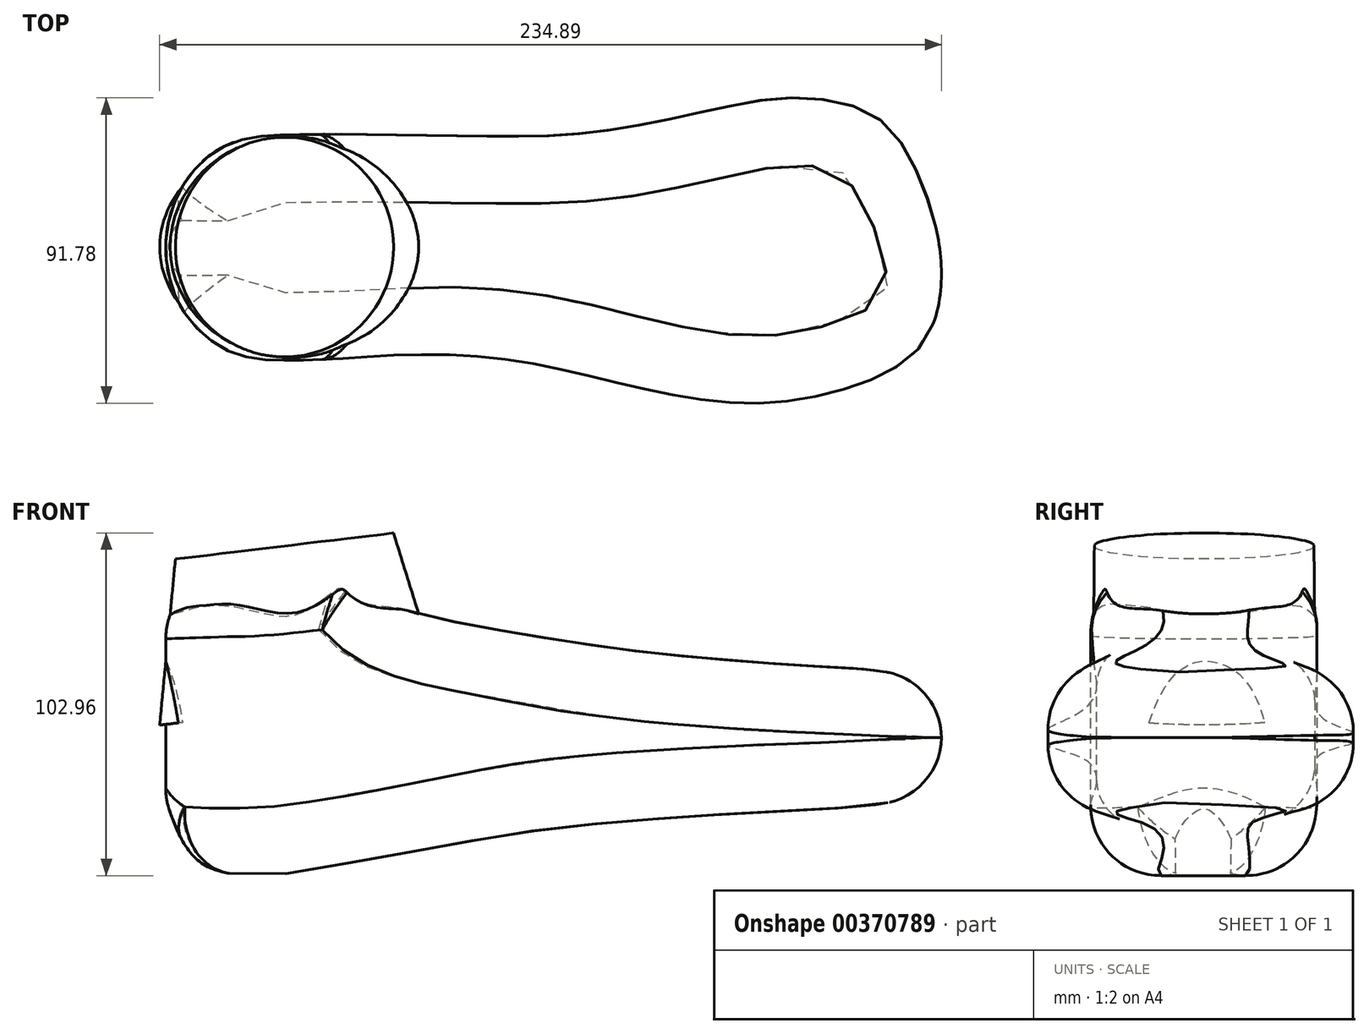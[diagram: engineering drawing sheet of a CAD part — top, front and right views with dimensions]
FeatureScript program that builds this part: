
annotation { "Feature Type Name" : "Feature", "Feature Type Description" : "" }
export const myFeature = defineFeature(function(context is Context, id is Id, definition is map)
    precondition{}
    {
        {
            var Q0;
            Q0=qCreatedBy(makeId("Top.planeOp"),FACE);
            cPlane(context, id + "F0", {"entities" : qUnion([Q0]), "cplaneType" : CPlaneType.OFFSET, "offset" : 10 * mm, "oppositeDirection" : true, "width" : 150 * mm, "height" : 150 * mm});
        }
        {
            var Q0;
            Q0=qCreatedBy(makeId("Front.planeOp"),FACE);
            var sketch = newSketch(context, id + "F1", { "sketchPlane" : qUnion([Q0])});
            skLineSegment(sketch, "E0", {"start": v(-126.2, 34.59) * mm, "end": v(0, 49.64) * mm, "construction": true});
            skSolve(sketch);
        }
        {
            var Q0;
            Q0=qCreatedBy(makeId("Right.planeOp"),FACE);
            var sketch = newSketch(context, id + "F2", { "sketchPlane" : qUnion([Q0])});
            skLineSegment(sketch, "E1.0", {"start": v(0, 34.59) * mm, "end": v(0, 49.64) * mm, "construction": true});
            skLineSegment(sketch, "E2", {"start": v(0, 49.64) * mm, "end": v(78.18, 49.64) * mm, "construction": true});
            skSolve(sketch);
        }
        {
            var Q0;
            Q0=sQuery(id+"F2.wireOp",VERTEX,"E2.end");
            var Q1;
            Q1=sQuery(id+"F2.wireOp",VERTEX,"E2.start");
            var Q2;
            Q2=sQuery(id+"F1.wireOp",VERTEX,"E0.start");
            cPlane(context, id + "F3", {"entities" : qUnion([Q0, Q1, Q2]), "cplaneType" : CPlaneType.THREE_POINT, "offset" : 25 * mm, "width" : 150 * mm, "height" : 150 * mm});
        }
        {
            var Q0;
            Q0=qCreatedBy(id+"F0.planeOp",FACE);
            cPlane(context, id + "F4", {"entities" : qUnion([Q0]), "cplaneType" : CPlaneType.OFFSET, "offset" : 70 * mm, "width" : 150 * mm, "height" : 150 * mm});
        }
        {
            var Q0;
            Q0=qCreatedBy(id+"F4.planeOp",FACE);
            var sketch = newSketch(context, id + "F5", { "sketchPlane" : qUnion([Q0])});
            skLineSegment(sketch, "E3.bottom", {"start": v(178, 87.04) * mm, "end": v(-168.77, 87.04) * mm});
            skLineSegment(sketch, "E3.top", {"start": v(178, -71.84) * mm, "end": v(-168.77, -71.84) * mm});
            skLineSegment(sketch, "E3.left", {"start": v(178, 87.04) * mm, "end": v(178, -71.84) * mm});
            skLineSegment(sketch, "E3.right", {"start": v(-168.77, 87.04) * mm, "end": v(-168.77, -71.84) * mm});
            skFitSpline(sketch, "E4", {"points": [v(111.8, -41.46) * mm, v(125.03, -30.87) * mm, v(130.33, -15.25) * mm, v(129.4, 3.7) * mm, v(122.2, 25.52) * mm, v(108.35, 43.13) * mm, v(83.24, 48.74) * mm, v(61.9, 46.12) * mm, v(19.97, 37.89) * mm, v(-18.8, 36.21) * mm, v(-53.4, 36.76) * mm, v(-76.61, 36.81) * mm, v(-99.24, 34.61) * mm, v(-114.06, 24.29) * mm, v(-122.11, 6.16) * mm, v(-120.89, -12.02) * mm, v(-114.25, -24.52) * mm, v(-104.4, -32.8) * mm, v(-93.42, -36.4) * mm, v(-70, -36.67) * mm, v(-39.87, -35.1) * mm, v(-3.08, -38.02) * mm, v(40.33, -47.81) * mm, v(79.5, -50.46) * mm, v(111.8, -41.46) * mm]});
            skSolve(sketch);
        }
        {
            var Q0;
            Q0=qCreatedBy(makeId("Front.planeOp"),FACE);
            var sketch = newSketch(context, id + "F6", { "sketchPlane" : qUnion([Q0])});
            skFitSpline(sketch, "E5", {"points": [v(-119.13, 38.44) * mm, v(-119.13, 33.94) * mm, v(-120.9, 4.27) * mm, v(-123.57, -25.48) * mm, v(-120.92, -39.45) * mm, v(-113.66, -52.87) * mm, v(-104.36, -58.06) * mm, v(-92.75, -59.32) * mm, v(-77.53, -57.75) * mm, v(-27.63, -48.8) * mm, v(12.86, -42.84) * mm, v(69.82, -38.75) * mm, v(100.89, -37.03) * mm, v(116.9, -34.52) * mm, v(127.68, -28.43) * mm, v(131.34, -21.72) * mm, v(132.41, -11.5) * mm, v(130.12, -3.1) * mm, v(121.42, 4.53) * mm, v(108.1, 7.85) * mm, v(96.18, 8.64) * mm, v(56.48, 11.46) * mm, v(17.18, 15.9) * mm, v(-22.2, 22.42) * mm, v(-50.23, 30.16) * mm, v(-57.52, 38.83) * mm, v(-59.94, 45.04) * mm, v(-66.68, 44.3) * mm, v(-113.57, 39.24) * mm, v(-119.13, 38.44) * mm]});
            skSolve(sketch);
        }
        {
            var Q0;
            Q0=qSketchRegion(id+"F6",true);
            extrude(context, id + "F7", {"entities" : qUnion([Q0]), "depth" : 140 * mm, "symmetric" : true});
        }
        {
            var Q0;
            Q0=makeQuery(id+"F5.imprint","IMPRINT",FACE,{"disambiguationData":[TD([[makeQuery(id+"F5.imprint","IMPRINT",EDGE,{"derivedFrom":sQuery(id+"F5.wireOp",EDGE,"E3.bottom")}),1.0]])]});
            extrude(context, id + "F8", {"entities" : qUnion([Q0]), "operationType" : NewBodyOperationType.REMOVE, "oppositeDirection" : true, "depth" : 130 * mm});
        }
        {
            var Q0;
            Q0=makeQuery(id+"F8.boolean.opBoolean","INTERSECT",EDGE,{"disambiguationData":[OD(1.0)],"derivedFrom":[makeQuery(id+"F7.opExtrude","SWEPT_FACE",FACE,{"disambiguationData":[OSD([sQuery(id+"F6.wireOp",EDGE,"E5")])]}),makeQuery(id+"F8.opExtrude","SWEPT_FACE",FACE,{"disambiguationData":[OSD([sQuery(id+"F5.wireOp",EDGE,"E4")])]})]});
            fillet(context, id + "F9", {"entities" : qUnion([Q0]), "radius" : 22 * mm, "allowEdgeOverflow" : false});
        }
        {
            var Q0;
            Q0=makeQuery(id+"F8.boolean.opBoolean","INTERSECT",EDGE,{"disambiguationData":[OD(0.0)],"derivedFrom":[makeQuery(id+"F7.opExtrude","SWEPT_FACE",FACE,{"disambiguationData":[OSD([sQuery(id+"F6.wireOp",EDGE,"E5")])]}),makeQuery(id+"F8.opExtrude","SWEPT_FACE",FACE,{"disambiguationData":[OSD([sQuery(id+"F5.wireOp",EDGE,"E4")])]})]});
            fillet(context, id + "F10", {"entities" : qUnion([Q0]), "radius" : 22 * mm, "tangentPropagation" : true, "allowEdgeOverflow" : false});
        }
        {
            var Q0;
            Q0=qCreatedBy(id+"F3.planeOp",FACE);
            var sketch = newSketch(context, id + "F11", { "sketchPlane" : qUnion([Q0])});
            skLineSegment(sketch, "E6.bottom", {"start": v(-167.37, -58.49) * mm, "end": v(31.87, -58.49) * mm});
            skLineSegment(sketch, "E6.top", {"start": v(-167.37, 81.96) * mm, "end": v(31.87, 81.96) * mm});
            skLineSegment(sketch, "E6.left", {"start": v(-167.37, -58.49) * mm, "end": v(-167.37, 81.96) * mm});
            skLineSegment(sketch, "E6.right", {"start": v(31.87, -58.49) * mm, "end": v(31.87, 81.96) * mm});
            skSolve(sketch);
        }
        {
            var Q0;
            Q0=makeQuery(id+"F11.imprint","IMPRINT",FACE,{"disambiguationData":[TD([[makeQuery(id+"F11.imprint","IMPRINT",EDGE,{"derivedFrom":sQuery(id+"F11.wireOp",EDGE,"E6.bottom")}),1.0]])]});
            extrude(context, id + "F12", {"entities" : qUnion([Q0]), "operationType" : NewBodyOperationType.REMOVE, "depth" : 10 * mm, "symmetric" : true});
        }
        {
            var Q0;
            Q0=qCreatedBy(id+"F3.planeOp",FACE);
            cPlane(context, id + "F13", {"entities" : qUnion([Q0]), "cplaneType" : CPlaneType.OFFSET, "offset" : 96 * mm, "oppositeDirection" : true, "width" : 150 * mm, "height" : 150 * mm});
        }
        {
            var Q0;
            Q0=qCreatedBy(id+"F13.planeOp",FACE);
            cPlane(context, id + "F14", {"entities" : qUnion([Q0]), "cplaneType" : CPlaneType.OFFSET, "offset" : 100 * mm, "width" : 150 * mm, "height" : 150 * mm});
        }
        {
            var Q0;
            Q0=qCreatedBy(id+"F3.planeOp",FACE);
            cPlane(context, id + "F15", {"entities" : qUnion([Q0]), "cplaneType" : CPlaneType.OFFSET, "offset" : 45 * mm, "oppositeDirection" : true, "width" : 150 * mm, "height" : 150 * mm});
        }
        {
            var Q0;
            Q0=qCreatedBy(id+"F15.planeOp",FACE);
            var sketch = newSketch(context, id + "F16", { "sketchPlane" : qUnion([Q0])});
            skEllipse(sketch, "E7", {"center": v(-72.11, 0) * mm, "majorRadius": 42.83 * mm, "minorRadius": 33.42 * mm, "majorAxis": v(1, 0)});
            skSolve(sketch);
        }
        {
            var Q0;
            Q0=makeQuery(id+"F7.opExtrude","SWEPT_BODY",BODY,{"disambiguationData":[OSD([sQuery(id+"F6.wireOp",EDGE,"E5")])]});
            var Q1;
            Q1=qCreatedBy(makeId("Origin.pointOp"),VERTEX);
            transform(context, id + "F17", {"entities" : qUnion([Q0]), "transformType" : TransformType.SCALE_UNIFORMLY, "scale" : 0.92, "scalePoint" : qUnion([Q1]), "makeCopy" : false});
        }
        {
            var Q0;
            Q0=qCreatedBy(id+"F14.planeOp",FACE);
            var sketch = newSketch(context, id + "F18", { "sketchPlane" : qUnion([Q0])});
            skCircle(sketch, "E8", {"center": v(-71.33, 0) * mm, "radius": 33 * mm});
            skSolve(sketch);
        }
        {
            var Q1;
            Q1=makeQuery(id+"F18.imprint","IMPRINT",FACE,{"disambiguationData":[TD([[makeQuery(id+"F18.imprint","IMPRINT",EDGE,{"derivedFrom":sQuery(id+"F18.wireOp",EDGE,"E8")}),1.0]])]});
            var Q2;
            Q2=makeQuery(id+"F16.imprint","IMPRINT",FACE,{"disambiguationData":[TD([[makeQuery(id+"F16.imprint","IMPRINT",EDGE,{"derivedFrom":sQuery(id+"F16.wireOp",EDGE,"E7")}),1.0]])]});
            loft(context, id + "F19", {"operationType" : NewBodyOperationType.ADD, "sheetProfilesArray" : [{ "sheetProfileEntities" : qUnion([Q1]) }, { "sheetProfileEntities" : qUnion([Q2]) }]});
        }
    });
